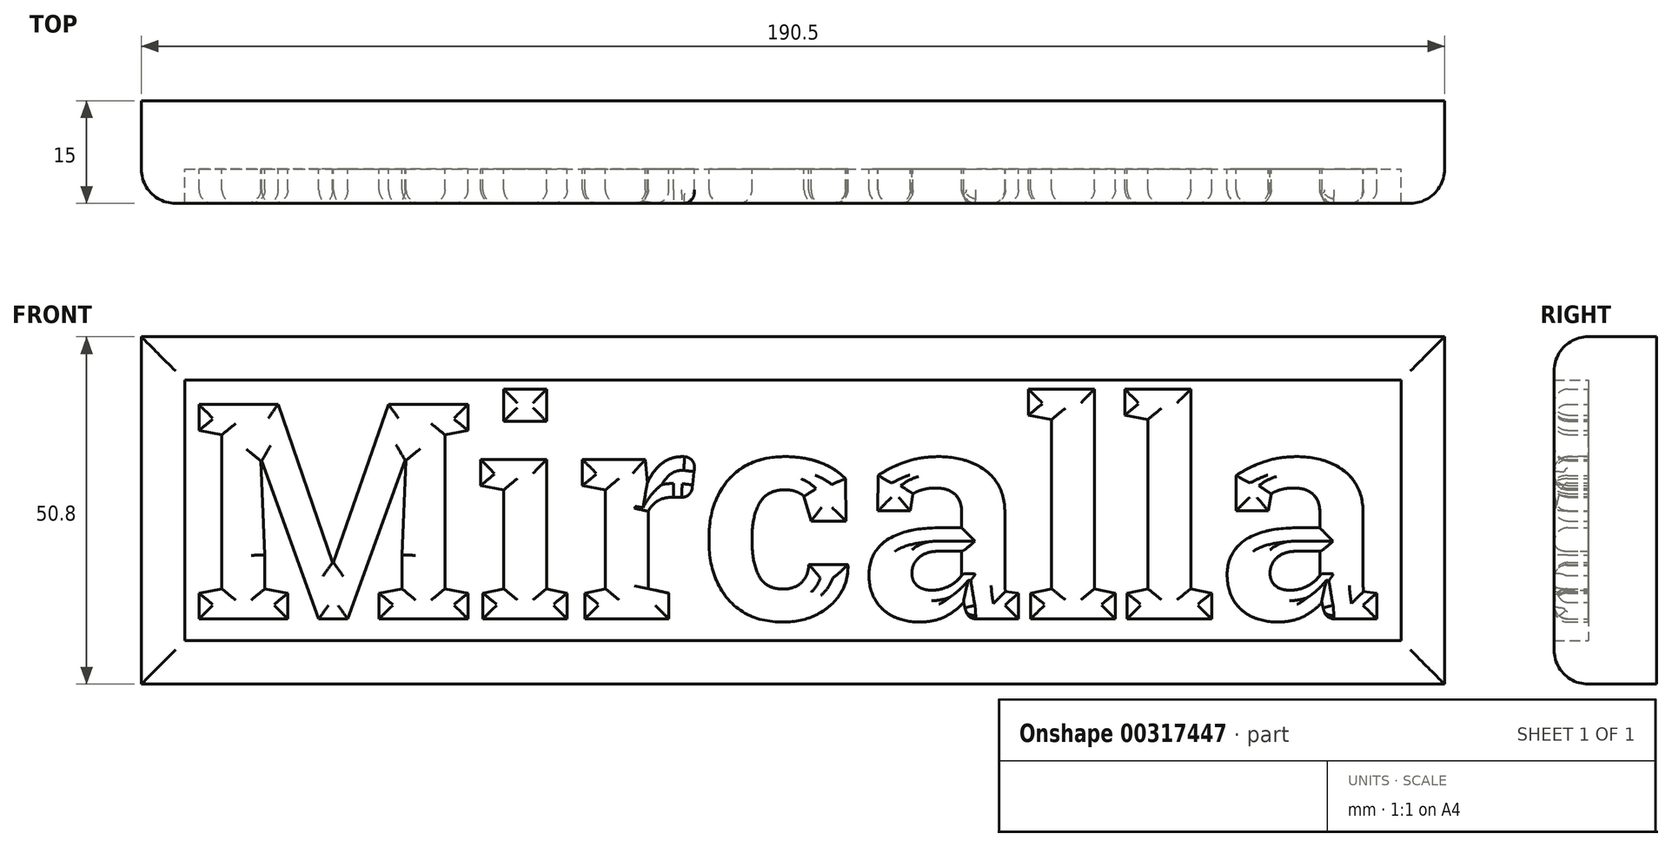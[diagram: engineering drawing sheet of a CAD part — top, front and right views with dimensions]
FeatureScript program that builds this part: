
annotation { "Feature Type Name" : "Feature", "Feature Type Description" : "" }
export const myFeature = defineFeature(function(context is Context, id is Id, definition is map)
    precondition{}
    {
        {
            var Q0;
            Q0=qCreatedBy(makeId("Front.planeOp"),FACE);
            var sketch = newSketch(context, id + "F0", { "sketchPlane" : qUnion([Q0])});
            skText(sketch, "E0", { "text": "Mircalla", "fontName": "RobotoSlab-Bold.ttf"});
            const initialGuessF0  = {"E0": [-0.08802, -0.01587, 1, 0, 0.03175]};
            skSetInitialGuess(sketch, initialGuessF0);
            skSolve(sketch);
        }
        {
            var Q0;
            Q0=qCreatedBy(makeId("Front.planeOp"),FACE);
            var sketch = newSketch(context, id + "F1", { "sketchPlane" : qUnion([Q0])});
            skLineSegment(sketch, "E1.bottom", {"start": v(-88.9, 19.05) * mm, "end": v(88.9, 19.05) * mm});
            skLineSegment(sketch, "E1.top", {"start": v(-88.9, -19.05) * mm, "end": v(88.9, -19.05) * mm});
            skLineSegment(sketch, "E1.left", {"start": v(-88.9, 19.05) * mm, "end": v(-88.9, -19.05) * mm});
            skLineSegment(sketch, "E1.right", {"start": v(88.9, 19.05) * mm, "end": v(88.9, -19.05) * mm});
            skLineSegment(sketch, "E2.bottom", {"start": v(-95.25, 25.4) * mm, "end": v(95.25, 25.4) * mm});
            skLineSegment(sketch, "E2.top", {"start": v(-95.25, -25.4) * mm, "end": v(95.25, -25.4) * mm});
            skLineSegment(sketch, "E2.left", {"start": v(-95.25, 25.4) * mm, "end": v(-95.25, -25.4) * mm});
            skLineSegment(sketch, "E2.right", {"start": v(95.25, 25.4) * mm, "end": v(95.25, -25.4) * mm});
            skSolve(sketch);
        }
        {
            var Q0;
            Q0=makeQuery(id+"F1.imprint","IMPRINT",FACE,{"disambiguationData":[TD([[makeQuery(id+"F1.imprint","IMPRINT",EDGE,{"derivedFrom":sQuery(id+"F1.wireOp",EDGE,"E1.bottom")}),-1.0]])]});
            var Q1;
            Q1=makeQuery(id+"F1.imprint","IMPRINT",FACE,{"disambiguationData":[TD([[makeQuery(id+"F1.imprint","IMPRINT",EDGE,{"derivedFrom":sQuery(id+"F1.wireOp",EDGE,"E1.bottom")}),1.0]])]});
            extrude(context, id + "F2", {"entities" : qUnion([Q0, Q1]), "oppositeDirection" : true, "depth" : 10 * mm});
        }
        {
            var Q0;
            Q0=qSketchRegion(id+"F1",true);
            extrude(context, id + "F3", {"entities" : qUnion([Q0]), "operationType" : NewBodyOperationType.ADD, "depth" : 5 * mm});
        }
        {
            var Q0;
            Q0=qSketchRegion(id+"F0",true);
            extrude(context, id + "F4", {"entities" : qUnion([Q0]), "operationType" : NewBodyOperationType.ADD, "depth" : 5 * mm});
        }
        {
            var Q0;
            Q0=makeQuery(id+"F3.opExtrude","CAP_EDGE",EDGE,{"disambiguationData":[OSD([sQuery(id+"F1.wireOp",EDGE,"E2.right")])],"isStart":false});
            var Q1;
            Q1=makeQuery(id+"F3.opExtrude","CAP_EDGE",EDGE,{"disambiguationData":[OSD([sQuery(id+"F1.wireOp",EDGE,"E2.left")])],"isStart":false});
            var Q2;
            Q2=makeQuery(id+"F3.opExtrude","CAP_EDGE",EDGE,{"disambiguationData":[OSD([sQuery(id+"F1.wireOp",EDGE,"E2.bottom")])],"isStart":false});
            var Q3;
            Q3=makeQuery(id+"F3.opExtrude","CAP_EDGE",EDGE,{"disambiguationData":[OSD([sQuery(id+"F1.wireOp",EDGE,"E2.top")])],"isStart":false});
            fillet(context, id + "F5", {"entities" : qUnion([Q0, Q1, Q2, Q3]), "radius" : 5 * mm, "tangentPropagation" : true, "allowEdgeOverflow" : false});
        }
        {
            var Q0;
            Q0=makeQuery(id+"F4.opExtrude","CAP_FACE",FACE,{"disambiguationData":[OSD([sQuery(id+"F0.wireOp",EDGE,"E0.sketch_text.stroke-0"),sQuery(id+"F0.wireOp",EDGE,"E0.sketch_text.stroke-1"),sQuery(id+"F0.wireOp",EDGE,"E0.sketch_text.stroke-2"),sQuery(id+"F0.wireOp",EDGE,"E0.sketch_text.stroke-3"),sQuery(id+"F0.wireOp",EDGE,"E0.sketch_text.stroke-4"),sQuery(id+"F0.wireOp",EDGE,"E0.sketch_text.stroke-5"),sQuery(id+"F0.wireOp",EDGE,"E0.sketch_text.stroke-6"),sQuery(id+"F0.wireOp",EDGE,"E0.sketch_text.stroke-7"),sQuery(id+"F0.wireOp",EDGE,"E0.sketch_text.stroke-8"),sQuery(id+"F0.wireOp",EDGE,"E0.sketch_text.stroke-9"),sQuery(id+"F0.wireOp",EDGE,"E0.sketch_text.stroke-10"),sQuery(id+"F0.wireOp",EDGE,"E0.sketch_text.stroke-11"),sQuery(id+"F0.wireOp",EDGE,"E0.sketch_text.stroke-12"),sQuery(id+"F0.wireOp",EDGE,"E0.sketch_text.stroke-13"),sQuery(id+"F0.wireOp",EDGE,"E0.sketch_text.stroke-14"),sQuery(id+"F0.wireOp",EDGE,"E0.sketch_text.stroke-15"),sQuery(id+"F0.wireOp",EDGE,"E0.sketch_text.stroke-16"),sQuery(id+"F0.wireOp",EDGE,"E0.sketch_text.stroke-17"),sQuery(id+"F0.wireOp",EDGE,"E0.sketch_text.stroke-18"),sQuery(id+"F0.wireOp",EDGE,"E0.sketch_text.stroke-19"),sQuery(id+"F0.wireOp",EDGE,"E0.sketch_text.stroke-20"),sQuery(id+"F0.wireOp",EDGE,"E0.sketch_text.stroke-21"),sQuery(id+"F0.wireOp",EDGE,"E0.sketch_text.stroke-22"),sQuery(id+"F0.wireOp",EDGE,"E0.sketch_text.stroke-23"),sQuery(id+"F0.wireOp",EDGE,"E0.sketch_text.stroke-24"),sQuery(id+"F0.wireOp",EDGE,"E0.sketch_text.stroke-25"),sQuery(id+"F0.wireOp",EDGE,"E0.sketch_text.stroke-26"),sQuery(id+"F0.wireOp",EDGE,"E0.sketch_text.stroke-27"),sQuery(id+"F0.wireOp",EDGE,"E0.sketch_text.stroke-28"),sQuery(id+"F0.wireOp",EDGE,"E0.sketch_text.stroke-29"),sQuery(id+"F0.wireOp",EDGE,"E0.sketch_text.stroke-30")])],"isStart":false});
            var Q1;
            Q1=makeQuery(id+"F4.opExtrude","CAP_FACE",FACE,{"disambiguationData":[OSD([sQuery(id+"F0.wireOp",EDGE,"E0.sketch_text.stroke-31"),sQuery(id+"F0.wireOp",EDGE,"E0.sketch_text.stroke-32"),sQuery(id+"F0.wireOp",EDGE,"E0.sketch_text.stroke-33"),sQuery(id+"F0.wireOp",EDGE,"E0.sketch_text.stroke-34"),sQuery(id+"F0.wireOp",EDGE,"E0.sketch_text.stroke-35"),sQuery(id+"F0.wireOp",EDGE,"E0.sketch_text.stroke-36"),sQuery(id+"F0.wireOp",EDGE,"E0.sketch_text.stroke-37"),sQuery(id+"F0.wireOp",EDGE,"E0.sketch_text.stroke-38"),sQuery(id+"F0.wireOp",EDGE,"E0.sketch_text.stroke-39"),sQuery(id+"F0.wireOp",EDGE,"E0.sketch_text.stroke-40")])],"isStart":false});
            var Q2;
            Q2=makeQuery(id+"F4.opExtrude","CAP_FACE",FACE,{"disambiguationData":[OSD([sQuery(id+"F0.wireOp",EDGE,"E0.sketch_text.stroke-41"),sQuery(id+"F0.wireOp",EDGE,"E0.sketch_text.stroke-42"),sQuery(id+"F0.wireOp",EDGE,"E0.sketch_text.stroke-43"),sQuery(id+"F0.wireOp",EDGE,"E0.sketch_text.stroke-44")])],"isStart":false});
            var Q3;
            Q3=makeQuery(id+"F4.opExtrude","CAP_FACE",FACE,{"disambiguationData":[OSD([sQuery(id+"F0.wireOp",EDGE,"E0.sketch_text.stroke-64"),sQuery(id+"F0.wireOp",EDGE,"E0.sketch_text.stroke-65"),sQuery(id+"F0.wireOp",EDGE,"E0.sketch_text.stroke-66"),sQuery(id+"F0.wireOp",EDGE,"E0.sketch_text.stroke-67"),sQuery(id+"F0.wireOp",EDGE,"E0.sketch_text.stroke-68"),sQuery(id+"F0.wireOp",EDGE,"E0.sketch_text.stroke-69"),sQuery(id+"F0.wireOp",EDGE,"E0.sketch_text.stroke-70"),sQuery(id+"F0.wireOp",EDGE,"E0.sketch_text.stroke-71"),sQuery(id+"F0.wireOp",EDGE,"E0.sketch_text.stroke-72"),sQuery(id+"F0.wireOp",EDGE,"E0.sketch_text.stroke-73"),sQuery(id+"F0.wireOp",EDGE,"E0.sketch_text.stroke-74"),sQuery(id+"F0.wireOp",EDGE,"E0.sketch_text.stroke-75"),sQuery(id+"F0.wireOp",EDGE,"E0.sketch_text.stroke-76"),sQuery(id+"F0.wireOp",EDGE,"E0.sketch_text.stroke-77"),sQuery(id+"F0.wireOp",EDGE,"E0.sketch_text.stroke-78"),sQuery(id+"F0.wireOp",EDGE,"E0.sketch_text.stroke-79"),sQuery(id+"F0.wireOp",EDGE,"E0.sketch_text.stroke-80"),sQuery(id+"F0.wireOp",EDGE,"E0.sketch_text.stroke-81"),sQuery(id+"F0.wireOp",EDGE,"E0.sketch_text.stroke-82"),sQuery(id+"F0.wireOp",EDGE,"E0.sketch_text.stroke-83"),sQuery(id+"F0.wireOp",EDGE,"E0.sketch_text.stroke-84"),sQuery(id+"F0.wireOp",EDGE,"E0.sketch_text.stroke-85"),sQuery(id+"F0.wireOp",EDGE,"E0.sketch_text.stroke-86")])],"isStart":false});
            var Q4;
            Q4=makeQuery(id+"F4.opExtrude","CAP_FACE",FACE,{"disambiguationData":[OSD([sQuery(id+"F0.wireOp",EDGE,"E0.sketch_text.stroke-122"),sQuery(id+"F0.wireOp",EDGE,"E0.sketch_text.stroke-123"),sQuery(id+"F0.wireOp",EDGE,"E0.sketch_text.stroke-124"),sQuery(id+"F0.wireOp",EDGE,"E0.sketch_text.stroke-125"),sQuery(id+"F0.wireOp",EDGE,"E0.sketch_text.stroke-126"),sQuery(id+"F0.wireOp",EDGE,"E0.sketch_text.stroke-127"),sQuery(id+"F0.wireOp",EDGE,"E0.sketch_text.stroke-128"),sQuery(id+"F0.wireOp",EDGE,"E0.sketch_text.stroke-129"),sQuery(id+"F0.wireOp",EDGE,"E0.sketch_text.stroke-130"),sQuery(id+"F0.wireOp",EDGE,"E0.sketch_text.stroke-131")])],"isStart":false});
            var Q5;
            Q5=makeQuery(id+"F4.opExtrude","CAP_FACE",FACE,{"disambiguationData":[OSD([sQuery(id+"F0.wireOp",EDGE,"E0.sketch_text.stroke-132"),sQuery(id+"F0.wireOp",EDGE,"E0.sketch_text.stroke-133"),sQuery(id+"F0.wireOp",EDGE,"E0.sketch_text.stroke-134"),sQuery(id+"F0.wireOp",EDGE,"E0.sketch_text.stroke-135"),sQuery(id+"F0.wireOp",EDGE,"E0.sketch_text.stroke-136"),sQuery(id+"F0.wireOp",EDGE,"E0.sketch_text.stroke-137"),sQuery(id+"F0.wireOp",EDGE,"E0.sketch_text.stroke-138"),sQuery(id+"F0.wireOp",EDGE,"E0.sketch_text.stroke-139"),sQuery(id+"F0.wireOp",EDGE,"E0.sketch_text.stroke-140"),sQuery(id+"F0.wireOp",EDGE,"E0.sketch_text.stroke-141")])],"isStart":false});
            fillet(context, id + "F6", {"entities" : qUnion([Q0, Q1, Q2, Q3, Q4, Q5]), "radius" : 2 * mm, "tangentPropagation" : true, "allowEdgeOverflow" : false});
        }
        {
            var Q0;
            Q0=makeQuery(id+"F4.opExtrude","CAP_EDGE",EDGE,{"disambiguationData":[OSD([sQuery(id+"F0.wireOp",EDGE,"E0.sketch_text.stroke-46")])],"isStart":false});
            var Q1;
            Q1=makeQuery(id+"F4.opExtrude","CAP_EDGE",EDGE,{"disambiguationData":[OSD([sQuery(id+"F0.wireOp",EDGE,"E0.sketch_text.stroke-59")])],"isStart":false});
            var Q2;
            Q2=makeQuery(id+"F4.opExtrude","CAP_EDGE",EDGE,{"disambiguationData":[OSD([sQuery(id+"F0.wireOp",EDGE,"E0.sketch_text.stroke-61")])],"isStart":false});
            var Q3;
            Q3=makeQuery(id+"F4.opExtrude","CAP_EDGE",EDGE,{"disambiguationData":[OSD([sQuery(id+"F0.wireOp",EDGE,"E0.sketch_text.stroke-62")])],"isStart":false});
            var Q4;
            Q4=makeQuery(id+"F4.opExtrude","CAP_EDGE",EDGE,{"disambiguationData":[OSD([sQuery(id+"F0.wireOp",EDGE,"E0.sketch_text.stroke-47")])],"isStart":false});
            var Q5;
            Q5=makeQuery(id+"F4.opExtrude","CAP_EDGE",EDGE,{"disambiguationData":[OSD([sQuery(id+"F0.wireOp",EDGE,"E0.sketch_text.stroke-48")])],"isStart":false});
            var Q6;
            Q6=makeQuery(id+"F4.opExtrude","CAP_EDGE",EDGE,{"disambiguationData":[OSD([sQuery(id+"F0.wireOp",EDGE,"E0.sketch_text.stroke-58")])],"isStart":false});
            var Q7;
            Q7=makeQuery(id+"F4.opExtrude","CAP_EDGE",EDGE,{"disambiguationData":[OSD([sQuery(id+"F0.wireOp",EDGE,"E0.sketch_text.stroke-49")])],"isStart":false});
            var Q8;
            Q8=makeQuery(id+"F4.opExtrude","CAP_EDGE",EDGE,{"disambiguationData":[OSD([sQuery(id+"F0.wireOp",EDGE,"E0.sketch_text.stroke-50")])],"isStart":false});
            var Q9;
            Q9=makeQuery(id+"F4.opExtrude","CAP_EDGE",EDGE,{"disambiguationData":[OSD([sQuery(id+"F0.wireOp",EDGE,"E0.sketch_text.stroke-51")])],"isStart":false});
            var Q10;
            Q10=makeQuery(id+"F4.opExtrude","CAP_EDGE",EDGE,{"disambiguationData":[OSD([sQuery(id+"F0.wireOp",EDGE,"E0.sketch_text.stroke-45")])],"isStart":false});
            var Q11;
            Q11=makeQuery(id+"F4.opExtrude","CAP_EDGE",EDGE,{"disambiguationData":[OSD([sQuery(id+"F0.wireOp",EDGE,"E0.sketch_text.stroke-63")])],"isStart":false});
            fillet(context, id + "F7", {"entities" : qUnion([Q0, Q1, Q2, Q3, Q4, Q5, Q6, Q7, Q8, Q9, Q10, Q11]), "radius" : 2 * mm, "tangentPropagation" : true, "allowEdgeOverflow" : false});
        }
        {
            var Q0;
            Q0=makeQuery(id+"F4.opExtrude","CAP_EDGE",EDGE,{"disambiguationData":[OSD([sQuery(id+"F0.wireOp",EDGE,"E0.sketch_text.stroke-101")])],"isStart":false});
            var Q1;
            Q1=makeQuery(id+"F4.opExtrude","CAP_EDGE",EDGE,{"disambiguationData":[OSD([sQuery(id+"F0.wireOp",EDGE,"E0.sketch_text.stroke-103")])],"isStart":false});
            var Q2;
            Q2=makeQuery(id+"F4.opExtrude","CAP_EDGE",EDGE,{"disambiguationData":[OSD([sQuery(id+"F0.wireOp",EDGE,"E0.sketch_text.stroke-113")])],"isStart":false});
            var Q3;
            Q3=makeQuery(id+"F4.opExtrude","CAP_EDGE",EDGE,{"disambiguationData":[OSD([sQuery(id+"F0.wireOp",EDGE,"E0.sketch_text.stroke-89")])],"isStart":false});
            var Q4;
            Q4=makeQuery(id+"F4.opExtrude","CAP_EDGE",EDGE,{"disambiguationData":[OSD([sQuery(id+"F0.wireOp",EDGE,"E0.sketch_text.stroke-116")])],"isStart":false});
            var Q5;
            Q5=makeQuery(id+"F4.opExtrude","CAP_EDGE",EDGE,{"disambiguationData":[OSD([sQuery(id+"F0.wireOp",EDGE,"E0.sketch_text.stroke-104")])],"isStart":false});
            var Q6;
            Q6=makeQuery(id+"F4.opExtrude","CAP_EDGE",EDGE,{"disambiguationData":[OSD([sQuery(id+"F0.wireOp",EDGE,"E0.sketch_text.stroke-111")])],"isStart":false});
            var Q7;
            Q7=makeQuery(id+"F4.opExtrude","CAP_EDGE",EDGE,{"disambiguationData":[OSD([sQuery(id+"F0.wireOp",EDGE,"E0.sketch_text.stroke-112")])],"isStart":false});
            var Q8;
            Q8=makeQuery(id+"F4.opExtrude","CAP_EDGE",EDGE,{"disambiguationData":[OSD([sQuery(id+"F0.wireOp",EDGE,"E0.sketch_text.stroke-96")])],"isStart":false});
            var Q9;
            Q9=makeQuery(id+"F4.opExtrude","CAP_EDGE",EDGE,{"disambiguationData":[OSD([sQuery(id+"F0.wireOp",EDGE,"E0.sketch_text.stroke-102")])],"isStart":false});
            var Q10;
            Q10=makeQuery(id+"F4.opExtrude","CAP_EDGE",EDGE,{"disambiguationData":[OSD([sQuery(id+"F0.wireOp",EDGE,"E0.sketch_text.stroke-144")])],"isStart":false});
            var Q11;
            Q11=makeQuery(id+"F4.opExtrude","CAP_EDGE",EDGE,{"disambiguationData":[OSD([sQuery(id+"F0.wireOp",EDGE,"E0.sketch_text.stroke-168")])],"isStart":false});
            var Q12;
            Q12=makeQuery(id+"F4.opExtrude","CAP_EDGE",EDGE,{"disambiguationData":[OSD([sQuery(id+"F0.wireOp",EDGE,"E0.sketch_text.stroke-171")])],"isStart":false});
            var Q13;
            Q13=makeQuery(id+"F4.opExtrude","CAP_EDGE",EDGE,{"disambiguationData":[OSD([sQuery(id+"F0.wireOp",EDGE,"E0.sketch_text.stroke-151")])],"isStart":false});
            var Q14;
            Q14=makeQuery(id+"F4.opExtrude","CAP_EDGE",EDGE,{"disambiguationData":[OSD([sQuery(id+"F0.wireOp",EDGE,"E0.sketch_text.stroke-159")])],"isStart":false});
            var Q15;
            Q15=makeQuery(id+"F4.opExtrude","CAP_EDGE",EDGE,{"disambiguationData":[OSD([sQuery(id+"F0.wireOp",EDGE,"E0.sketch_text.stroke-158")])],"isStart":false});
            var Q16;
            Q16=makeQuery(id+"F4.opExtrude","CAP_EDGE",EDGE,{"disambiguationData":[OSD([sQuery(id+"F0.wireOp",EDGE,"E0.sketch_text.stroke-157")])],"isStart":false});
            var Q17;
            Q17=makeQuery(id+"F4.opExtrude","CAP_EDGE",EDGE,{"disambiguationData":[OSD([sQuery(id+"F0.wireOp",EDGE,"E0.sketch_text.stroke-156")])],"isStart":false});
            var Q18;
            Q18=makeQuery(id+"F4.opExtrude","CAP_EDGE",EDGE,{"disambiguationData":[OSD([sQuery(id+"F0.wireOp",EDGE,"E0.sketch_text.stroke-166")])],"isStart":false});
            var Q19;
            Q19=makeQuery(id+"F4.opExtrude","CAP_EDGE",EDGE,{"disambiguationData":[OSD([sQuery(id+"F0.wireOp",EDGE,"E0.sketch_text.stroke-167")])],"isStart":false});
            fillet(context, id + "F8", {"entities" : qUnion([Q0, Q1, Q2, Q3, Q4, Q5, Q6, Q7, Q8, Q9, Q10, Q11, Q12, Q13, Q14, Q15, Q16, Q17, Q18, Q19]), "radius" : 2 * mm, "tangentPropagation" : true, "allowEdgeOverflow" : false});
        }
        {
            var Q0;
            Q0=makeQuery(id+"F4.opExtrude","CAP_EDGE",EDGE,{"disambiguationData":[OSD([sQuery(id+"F0.wireOp",EDGE,"E0.sketch_text.stroke-117")])],"isStart":false});
            var Q1;
            Q1=makeQuery(id+"F8.opFillet","BLEND_EDGE",EDGE,{"blendedFrom":[makeQuery(id+"F4.opExtrude","CAP_EDGE",EDGE,{"disambiguationData":[OSD([sQuery(id+"F0.wireOp",EDGE,"E0.sketch_text.stroke-113")])],"isStart":false}),makeQuery(id+"F4.opExtrude","SWEPT_FACE",FACE,{"disambiguationData":[OSD([sQuery(id+"F0.wireOp",EDGE,"E0.sketch_text.stroke-87")])]})],"blendedInto":[makeQuery(id+"F4.opExtrude","SWEPT_FACE",FACE,{"disambiguationData":[OSD([sQuery(id+"F0.wireOp",EDGE,"E0.sketch_text.stroke-87")])]})]});
            var Q2;
            Q2=makeQuery(id+"F4.opExtrude","CAP_EDGE",EDGE,{"disambiguationData":[OSD([sQuery(id+"F0.wireOp",EDGE,"E0.sketch_text.stroke-172")])],"isStart":false});
            var Q3;
            Q3=makeQuery(id+"F8.opFillet","BLEND_EDGE",EDGE,{"blendedFrom":[makeQuery(id+"F4.opExtrude","CAP_EDGE",EDGE,{"disambiguationData":[OSD([sQuery(id+"F0.wireOp",EDGE,"E0.sketch_text.stroke-168")])],"isStart":false}),makeQuery(id+"F4.opExtrude","SWEPT_FACE",FACE,{"disambiguationData":[OSD([sQuery(id+"F0.wireOp",EDGE,"E0.sketch_text.stroke-142")])]})],"blendedInto":[makeQuery(id+"F4.opExtrude","SWEPT_FACE",FACE,{"disambiguationData":[OSD([sQuery(id+"F0.wireOp",EDGE,"E0.sketch_text.stroke-142")])]})]});
            var Q4;
            Q4=makeQuery(id+"F4.opExtrude","CAP_EDGE",EDGE,{"disambiguationData":[OSD([sQuery(id+"F0.wireOp",EDGE,"E0.sketch_text.stroke-55")])],"isStart":false});
            fillet(context, id + "F9", {"entities" : qUnion([Q0, Q1, Q2, Q3, Q4]), "radius" : 1.52 * mm, "tangentPropagation" : true, "allowEdgeOverflow" : false});
        }
    });
